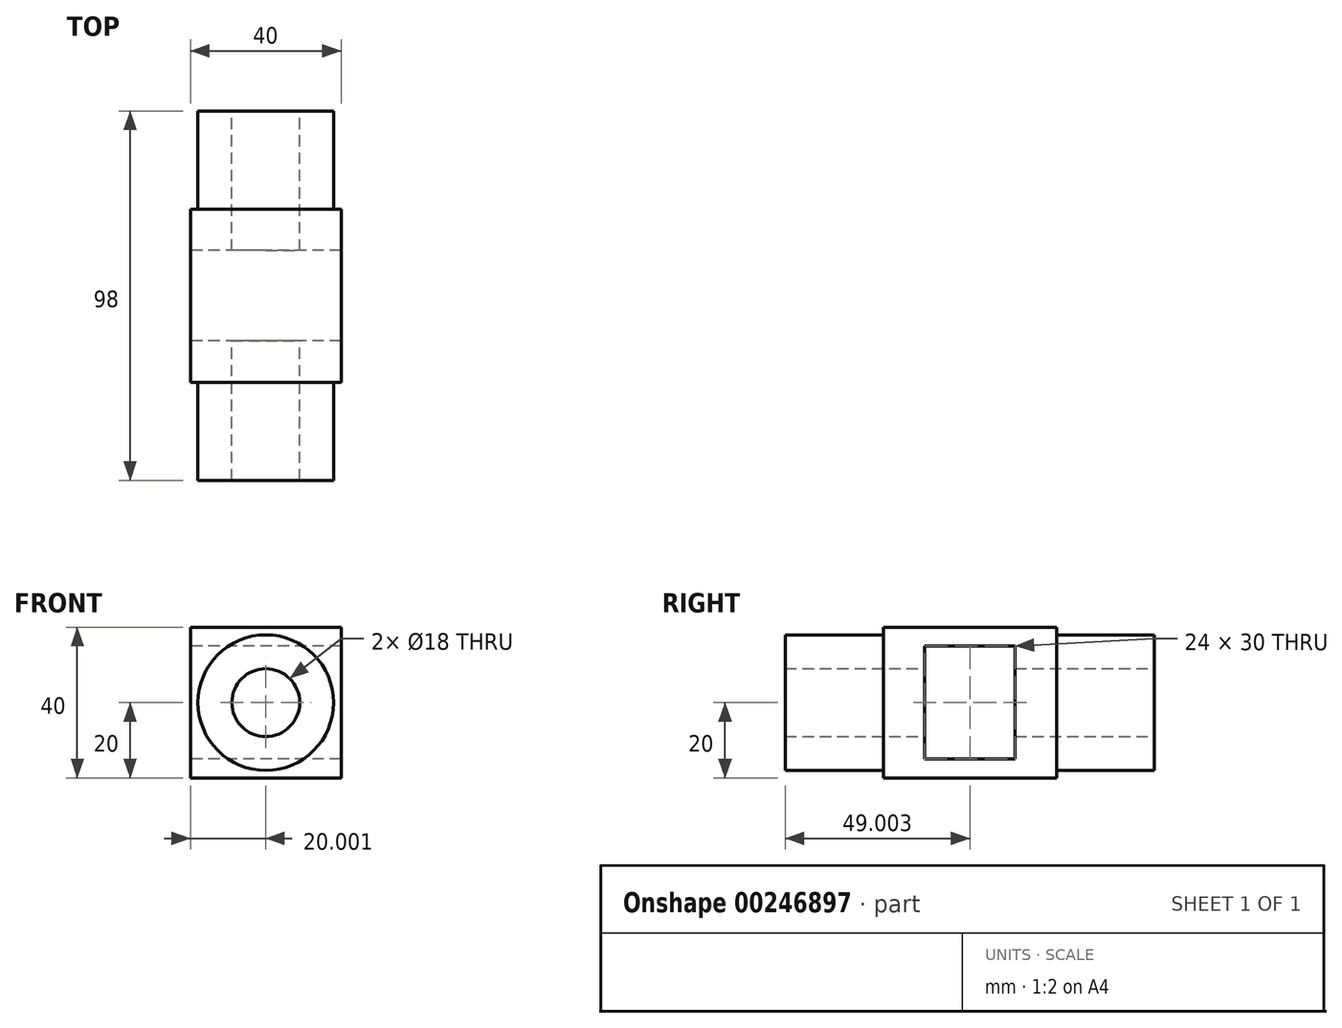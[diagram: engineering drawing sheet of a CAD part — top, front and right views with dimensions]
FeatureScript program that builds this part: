
annotation { "Feature Type Name" : "Feature", "Feature Type Description" : "" }
export const myFeature = defineFeature(function(context is Context, id is Id, definition is map)
    precondition{}
    {
        {
            var Q0;
            Q0=qCreatedBy(makeId("Top.planeOp"),FACE);
            var sketch = newSketch(context, id + "F0", { "sketchPlane" : qUnion([Q0])});
            skLineSegment(sketch, "E0.bottom", {"start": v(-74.4, -72.86) * mm, "end": v(-34.4, -72.86) * mm});
            skLineSegment(sketch, "E0.top", {"start": v(-74.4, -26.86) * mm, "end": v(-34.4, -26.86) * mm});
            skLineSegment(sketch, "E0.left", {"start": v(-74.4, -72.86) * mm, "end": v(-74.4, -26.86) * mm});
            skLineSegment(sketch, "E0.right", {"start": v(-34.4, -72.86) * mm, "end": v(-34.4, -26.86) * mm});
            skSolve(sketch);
        }
        {
            var Q0;
            Q0=makeQuery(id+"F0.imprint","IMPRINT",FACE,{"disambiguationData":[TD([[makeQuery(id+"F0.imprint","IMPRINT",EDGE,{"derivedFrom":sQuery(id+"F0.wireOp",EDGE,"E0.bottom")}),1.0]])]});
            extrude(context, id + "F1", {"entities" : qUnion([Q0]), "depth" : 40 * mm});
        }
        {
            var Q0;
            Q0=makeQuery(id+"F1.opExtrude","SWEPT_FACE",FACE,{"disambiguationData":[OSD([sQuery(id+"F0.wireOp",EDGE,"E0.bottom")])]});
            var sketch = newSketch(context, id + "F2", { "sketchPlane" : qUnion([Q0])});
            skCircle(sketch, "E1", {"center": v(-54.4, 20) * mm, "radius": 18 * mm});
            skPoint(sketch, "E1.centerSnap0", {"position": v(-54.4, 0) * mm});
            skPoint(sketch, "E1.centerSnap1", {"position": v(-34.4, 20) * mm});
            skSolve(sketch);
        }
        {
            var Q0;
            Q0=makeQuery(id+"F2.imprint","IMPRINT",FACE,{"disambiguationData":[TD([[makeQuery(id+"F2.imprint","IMPRINT",EDGE,{"derivedFrom":sQuery(id+"F2.wireOp",EDGE,"E1")}),1.0]])]});
            extrude(context, id + "F3", {"entities" : qUnion([Q0]), "operationType" : NewBodyOperationType.ADD, "depth" : 26 * mm});
        }
        {
            var Q0;
            Q0=makeQuery(id+"F1.opExtrude","SWEPT_FACE",FACE,{"disambiguationData":[OSD([sQuery(id+"F0.wireOp",EDGE,"E0.top")])]});
            var sketch = newSketch(context, id + "F4", { "sketchPlane" : qUnion([Q0])});
            skCircle(sketch, "E2", {"center": v(54.4, 20) * mm, "radius": 18 * mm});
            skPoint(sketch, "E2.centerSnap0", {"position": v(54.4, 0) * mm});
            skPoint(sketch, "E2.centerSnap1", {"position": v(34.4, 20) * mm});
            skSolve(sketch);
        }
        {
            var Q0;
            Q0=makeQuery(id+"F4.imprint","IMPRINT",FACE,{"disambiguationData":[TD([[makeQuery(id+"F4.imprint","IMPRINT",EDGE,{"derivedFrom":sQuery(id+"F4.wireOp",EDGE,"E2")}),1.0]])]});
            extrude(context, id + "F5", {"entities" : qUnion([Q0]), "operationType" : NewBodyOperationType.ADD, "depth" : 26 * mm});
        }
        {
            var Q0;
            Q0=makeQuery(id+"F1.opExtrude","SWEPT_FACE",FACE,{"disambiguationData":[OSD([sQuery(id+"F0.wireOp",EDGE,"E0.left")])]});
            var sketch = newSketch(context, id + "F6", { "sketchPlane" : qUnion([Q0])});
            skLineSegment(sketch, "E3.bottom", {"start": v(37.86, 5) * mm, "end": v(61.86, 5) * mm});
            skLineSegment(sketch, "E3.top", {"start": v(37.86, 35) * mm, "end": v(61.86, 35) * mm});
            skLineSegment(sketch, "E3.left", {"start": v(37.86, 5) * mm, "end": v(37.86, 35) * mm});
            skLineSegment(sketch, "E3.right", {"start": v(61.86, 5) * mm, "end": v(61.86, 35) * mm});
            skPoint(sketch, "E3.middle", {"position": v(49.86, 20) * mm});
            skPoint(sketch, "E3.middle.positionSnap0", {"position": v(49.86, 40) * mm});
            skPoint(sketch, "E3.middle.positionSnap1", {"position": v(72.86, 20) * mm});
            skPoint(sketch, "E3.centerSnap0", {"position": v(49.86, 40) * mm});
            skPoint(sketch, "E3.centerSnap1", {"position": v(72.86, 20) * mm});
            skSolve(sketch);
        }
        {
            var Q0;
            Q0=makeQuery(id+"F5.opExtrude","CAP_FACE",FACE,{"disambiguationData":[OSD([sQuery(id+"F4.wireOp",EDGE,"E2")])],"isStart":false});
            var sketch = newSketch(context, id + "F7", { "sketchPlane" : qUnion([Q0])});
            skCircle(sketch, "E4", {"center": v(54.4, 20) * mm, "radius": 9 * mm});
            skSolve(sketch);
        }
        {
            var Q0;
            Q0=sQuery(id+"F7.wireOp",VERTEX,"E4.center");
            var Q1;
            Q1=makeQuery(id+"F1.opExtrude","SWEPT_BODY",BODY,{"disambiguationData":[OSD([sQuery(id+"F0.wireOp",EDGE,"E0.bottom"),sQuery(id+"F0.wireOp",EDGE,"E0.top"),sQuery(id+"F0.wireOp",EDGE,"E0.left"),sQuery(id+"F0.wireOp",EDGE,"E0.right")])]});
            hole(context, id + "F8", {"style" : HoleStyle.SIMPLE, "endStyle" : HoleEndStyle.THROUGH, "holeDiameter" : 18 * mm, "tappedDepth" : 12 * mm, "tapClearance" : 3, "locations" : qUnion([Q0]), "scope" : qUnion([Q1])});
        }
        {
            var Q0;
            Q0=makeQuery(id+"F6.imprint","IMPRINT",FACE,{"disambiguationData":[TD([[makeQuery(id+"F6.imprint","IMPRINT",EDGE,{"derivedFrom":sQuery(id+"F6.wireOp",EDGE,"E3.bottom")}),1.0]])]});
            extrude(context, id + "F9", {"entities" : qUnion([Q0]), "operationType" : NewBodyOperationType.REMOVE, "oppositeDirection" : true, "depth" : 50 * mm});
        }
    });
